# Revit family: VAB_Horizontal_Ceiling_Mount
name_source: partatom
category: Mechanical Equipment
units: mm (PartAtom-declared; Revit-internal decimal feet)

## family parameters
Always vertical = Yes
Cut with Voids When Loaded = No
Part Type = Normal
Room Calculation Point = No
Round Connector Dimension = Use Radius
Shared = No
Work Plane-Based = No

## types (11) — shared parameters
0 = 0' - 0"
1" = 0' - 1"
1.5 = 0' - 1 1/2"
2" = 0' - 2"
2' = 2' - 0"
3" = 0' - 3"
30 = 30.00°
4" = 0' - 4"
6 = 0' - 6"
60 = 60.00°
Manufacturer = Loren Cook Company
Model = VAB
ONE EIGTH = 0' - 0 1/8"
Type Comments = Fixed Pitch Vane Axial Horizontal Ceiling Mount Belt Drive Arrangement 9
URL = www.lorencook.com
ZERO = 0' - 0"

## per-type parameters (varying)
- 12_VAB_HOR_CEILING: (A+.25")/2=0' - 6 1/8"; (E-.25")/2=0' - 9 7/8"; (H-(A/2))/2=0' - 7 1/2"; -(E-.25")/2=-0' - 9 7/8"; -E/2=-0' - 10"; A=1' - 0"; A/2=0' - 6"; A/3=0' - 4 13/16"; B=1' - 2 3/4"; B/2=0' - 7 3/8"; C=1' - 1 3/8"; C/2=0' - 6 11/16"; C/2+L=0' - 6 11/16"; E=1' - 8"; E-2"=1' - 6"; E/2=0' - 10"; F=0' - 0 5/16"; F/2=0' - 0 5/32"; G=6' - 0"; H=1' - 9"; H+L=1' - 9"; H-(A/2)=1' - 3"; J=1' - 8 5/16"; J-A=0' - 7 5/16"; J/2=0' - 10 5/32"; K=0' - 3 1/2"; K-((J-A)/2)=0' - 0 1/2"; K/2=0' - 1 3/4"; L=1' - 1"; L-(C/2)=-0' - 6 11/16"; L/2=0' - 6 1/2"; M=0' - 0 7/16"; M/2=0' - 0 7/32"
- 14_VAB_HOR_CEILING: (A+.25")/2=0' - 7 1/8"; (E-.25")/2=0' - 11 3/8"; (H-(A/2))/2=0' - 8 1/2"; -(E-.25")/2=-0' - 11 3/8"; -E/2=-0' - 11 1/2"; A=1' - 2"; A/2=0' - 7"; A/3=0' - 5 19/32"; B=1' - 4 3/4"; B/2=0' - 8 3/8"; C=1' - 3 1/2"; C/2=0' - 7 3/4"; C/2+L=0' - 7 3/4"; E=1' - 11"; E-2"=1' - 9"; E/2=0' - 11 1/2"; F=0' - 0 5/16"; F/2=0' - 0 5/32"; G=6' - 0"; H=2' - 0"; H+L=2' - 0"; H-(A/2)=1' - 5"; J=1' - 7 1/16"; J-A=0' - 4 1/16"; J/2=0' - 9 17/32"; K=0' - 3 1/2"; K-((J-A)/2)=0' - 0 1/2"; K/2=0' - 1 3/4"; L=1' - 4"; L-(C/2)=-0' - 7 3/4"; L/2=0' - 8"; M=0' - 0 7/16"; M/2=0' - 0 7/32"
- 18_VAB_HOR_CEILING: (A+.25")/2=0' - 9 1/8"; (E-.25")/2=1' - 2 3/8"; (H-(A/2))/2=0' - 9 1/8"; -(E-.25")/2=-1' - 2 3/8"; -E/2=-1' - 2 1/2"; A=1' - 6"; A/2=0' - 9"; A/3=0' - 7 3/16"; B=1' - 9 1/4"; B/2=0' - 10 5/8"; C=1' - 7 3/4"; C/2=0' - 9 7/8"; C/2+L=0' - 9 7/8"; E=2' - 5"; E-2"=2' - 3"; E/2=1' - 2 1/2"; F=0' - 0 7/16"; F/2=0' - 0 7/32"; G=12' - 0"; H=2' - 3 1/4"; H+L=2' - 3 1/4"; H-(A/2)=1' - 6 1/4"; J=2' - 1 1/4"; J-A=0' - 6 1/4"; J/2=1' - 0 5/8"; K=0' - 3 3/4"; K-((J-A)/2)=0' - 0 3/4"; K/2=0' - 1 7/8"; L=1' - 9 1/2"; L-(C/2)=-0' - 9 7/8"; L/2=0' - 10 3/4"; M=0' - 0 11/16"; M/2=0' - 0 11/32"
- 21_VAB_HOR_CEILING: (A+.25")/2=0' - 10 5/8"; (E-.25")/2=1' - 3 3/8"; (H-(A/2))/2=0' - 10 1/2"; -(E-.25")/2=-1' - 3 3/8"; -E/2=-1' - 3 1/2"; A=1' - 9"; A/2=0' - 10 1/2"; A/3=0' - 8 13/32"; B=2' - 0 1/4"; B/2=1' - 0 1/8"; C=1' - 10 3/4"; C/2=0' - 11 3/8"; C/2+L=0' - 11 3/8"; E=2' - 7"; E-2"=2' - 5"; E/2=1' - 3 1/2"; F=0' - 0 7/16"; F/2=0' - 0 7/32"; G=12' - 0"; H=2' - 7 1/2"; H+L=2' - 7 1/2"; H-(A/2)=1' - 9"; J=2' - 2 3/16"; J-A=0' - 4 3/16"; J/2=1' - 1 3/32"; K=0' - 3 3/4"; K-((J-A)/2)=0' - 0 3/4"; K/2=0' - 1 7/8"; L=1' - 11 1/2"; L-(C/2)=-0' - 11 3/8"; L/2=0' - 11 3/4"; M=0' - 0 11/16"; M/2=0' - 0 11/32"
- 26_VAB_HOR_CEILING: (A+.25")/2=1' - 1 1/8"; (E-.25")/2=1' - 3 7/8"; (H-(A/2))/2=0' - 10 3/4"; -(E-.25")/2=-1' - 3 7/8"; -E/2=-1' - 4"; A=2' - 2"; A/2=1' - 1"; A/3=0' - 10 13/32"; B=2' - 6 5/16"; B/2=1' - 3 5/32"; C=2' - 4"; C/2=1' - 2"; C/2+L=1' - 2"; E=2' - 8"; E-2"=2' - 6"; E/2=1' - 4"; F=0' - 0 7/16"; F/2=0' - 0 7/32"; G=12' - 0"; H=2' - 10 1/2"; H+L=2' - 10 1/2"; H-(A/2)=1' - 9 1/2"; J=2' - 5 13/16"; J-A=0' - 2 13/16"; J/2=1' - 2 29/32"; K=0' - 4 1/4"; K-((J-A)/2)=0' - 1 1/4"; K/2=0' - 2 1/8"; L=1' - 11 1/2"; L-(C/2)=-1' - 2"; L/2=0' - 11 3/4"; M=0' - 0 11/16"; M/2=0' - 0 11/32"
- 29_VAB_HOR_CEILING: (A+.25")/2=1' - 2 5/8"; (E-.25")/2=1' - 5 7/8"; (H-(A/2))/2=1' - 1"; -(E-.25")/2=-1' - 5 7/8"; -E/2=-1' - 6"; A=2' - 5"; A/2=1' - 2 1/2"; A/3=0' - 11 19/32"; B=2' - 9 5/16"; B/2=1' - 4 21/32"; C=2' - 7"; C/2=1' - 3 1/2"; C/2+L=1' - 3 1/2"; E=3' - 0"; E-2"=2' - 10"; E/2=1' - 6"; F=0' - 0 7/16"; F/2=0' - 0 7/32"; G=12' - 0"; H=3' - 4 1/2"; H+L=3' - 4 1/2"; H-(A/2)=2' - 2"; J=2' - 10 5/16"; J-A=0' - 4 5/16"; J/2=1' - 5 5/32"; K=0' - 4 1/4"; K-((J-A)/2)=0' - 1 1/4"; K/2=0' - 2 1/8"; L=2' - 3 1/2"; L-(C/2)=-1' - 3 1/2"; L/2=1' - 1 3/4"; M=0' - 0 11/16"; M/2=0' - 0 11/32"
- 36_VAB_HOR_CEILING: (A+.25")/2=1' - 6 1/8"; (E-.25")/2=1' - 8 7/8"; (H-(A/2))/2=1' - 1 3/4"; -(E-.25")/2=-1' - 8 7/8"; -E/2=-1' - 9"; A=3' - 0"; A/2=1' - 6"; A/3=1' - 2 13/32"; B=3' - 4 5/16"; B/2=1' - 8 5/32"; C=3' - 2"; C/2=1' - 7"; C/2+L=1' - 7"; E=3' - 6"; E-2"=3' - 4"; E/2=1' - 9"; F=0' - 0 9/16"; F/2=0' - 0 9/32"; G=16' - 0"; H=3' - 9 1/2"; H+L=3' - 9 1/2"; H-(A/2)=2' - 3 1/2"; J=3' - 3 3/4"; J-A=0' - 2 3/4"; J/2=1' - 7 7/8"; K=0' - 4 5/8"; K-((J-A)/2)=0' - 1 5/8"; K/2=0' - 2 5/16"; L=2' - 8 3/4"; L-(C/2)=-1' - 7"; L/2=1' - 4 3/8"; M=0' - 0 7/8"; M/2=0' - 0 7/16"
- 42_VAB_HOR_CEILING: (A+.25")/2=1' - 9 1/8"; (E-.25")/2=2' - 0 7/8"; (H-(A/2))/2=1' - 2 3/4"; -(E-.25")/2=-2' - 0 7/8"; -E/2=-2' - 1"; A=3' - 6"; A/2=1' - 9"; A/3=1' - 4 13/16"; B=3' - 9 5/16"; B/2=1' - 10 21/32"; C=3' - 8 3/8"; C/2=1' - 10 3/16"; C/2+L=1' - 10 3/16"; E=4' - 2"; E-2"=4' - 0"; E/2=2' - 1"; F=0' - 0 9/16"; F/2=0' - 0 9/32"; G=16' - 0"; H=4' - 2 1/2"; H+L=4' - 2 1/2"; H-(A/2)=2' - 5 1/2"; J=3' - 9 3/4"; J-A=0' - 2 3/4"; J/2=1' - 10 7/8"; K=0' - 4 5/8"; K-((J-A)/2)=0' - 1 5/8"; K/2=0' - 2 5/16"; L=3' - 4 3/4"; L-(C/2)=-1' - 10 3/16"; L/2=1' - 8 3/8"; M=0' - 0 7/8"; M/2=0' - 0 7/16"
- 48_VAB_HOR_CEILING: (A+.25")/2=2' - 0 1/8"; (E-.25")/2=2' - 3 7/8"; (H-(A/2))/2=1' - 3"; -(E-.25")/2=-2' - 3 7/8"; -E/2=-2' - 4"; A=4' - 0"; A/2=2' - 0"; A/3=1' - 7 3/16"; B=4' - 5 3/16"; B/2=2' - 2 19/32"; C=4' - 2 1/2"; C/2=2' - 1 1/4"; C/2+L=2' - 1 1/4"; E=4' - 8"; E-2"=4' - 6"; E/2=2' - 4"; F=0' - 0 9/16"; F/2=0' - 0 9/32"; G=16' - 0"; H=4' - 6"; H+L=4' - 6"; H-(A/2)=2' - 6"; J=4' - 3 3/4"; J-A=0' - 2 3/4"; J/2=2' - 1 7/8"; K=0' - 5 1/8"; K-((J-A)/2)=0' - 2 1/8"; K/2=0' - 2 9/16"; L=3' - 9 3/4"; L-(C/2)=-2' - 1 1/4"; L/2=1' - 10 7/8"; M=0' - 0 7/8"; M/2=0' - 0 7/16"
- 54_VAB_HOR_CEILING: (A+.25")/2=2' - 3 1/8"; (E-.25")/2=2' - 6 7/8"; (H-(A/2))/2=1' - 4 1/4"; -(E-.25")/2=-2' - 6 7/8"; -E/2=-2' - 7"; A=4' - 6"; A/2=2' - 3"; A/3=1' - 9 19/32"; B=4' - 11 7/16"; B/2=2' - 5 23/32"; C=4' - 8 1/2"; C/2=2' - 4 1/4"; C/2+L=2' - 4 1/4"; E=5' - 2"; E-2"=5' - 0"; E/2=2' - 7"; F=0' - 0 9/16"; F/2=0' - 0 9/32"; G=16' - 0"; H=4' - 11 1/2"; H+L=4' - 11 1/2"; H-(A/2)=2' - 8 1/2"; J=4' - 10 3/4"; J-A=0' - 3 3/4"; J/2=2' - 5 3/8"; K=0' - 5 5/8"; K-((J-A)/2)=0' - 2 5/8"; K/2=0' - 2 13/16"; L=4' - 2 3/4"; L-(C/2)=-2' - 4 1/4"; L/2=2' - 1 3/8"; M=0' - 1 1/16"; M/2=0' - 0 17/32"
- 60_VAB_HOR_CEILING: (A+.25")/2=2' - 6 1/8"; (E-.25")/2=2' - 10 3/8"; (H-(A/2))/2=1' - 5 1/2"; -(E-.25")/2=-2' - 10 3/8"; -E/2=-2' - 10 1/2"; A=5' - 0"; A/2=2' - 6"; A/3=2' - 0"; B=5' - 5 7/16"; B/2=2' - 8 23/32"; C=5' - 3 1/4"; C/2=2' - 7 5/8"; C/2+L=2' - 7 5/8"; E=5' - 9"; E-2"=5' - 7"; E/2=2' - 10 1/2"; F=0' - 0 9/16"; F/2=0' - 0 9/32"; G=16' - 0"; H=5' - 5"; H+L=5' - 5"; H-(A/2)=2' - 11"; J=5' - 4 3/4"; J-A=0' - 3 3/4"; J/2=2' - 8 3/8"; K=0' - 5 5/8"; K-((J-A)/2)=0' - 2 5/8"; K/2=0' - 2 13/16"; L=4' - 9 3/4"; L-(C/2)=-2' - 7 5/8"; L/2=2' - 4 7/8"; M=0' - 1 1/16"; M/2=0' - 0 17/32"

## geometry (parser evidence)
native form markers: Sweep x1
no freeform markers — native parametric forms only
